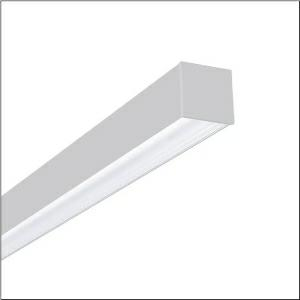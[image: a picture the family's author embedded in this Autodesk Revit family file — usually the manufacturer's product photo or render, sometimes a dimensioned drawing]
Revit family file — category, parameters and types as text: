
# Revit family: silica_r_5mx31bd1w4a_74d2
name_source: partatom
category: Lighting Fixtures
units: mm (PartAtom-declared; Revit-internal decimal feet)

## family parameters
Cut with Voids When Loaded = No
Host = Face
Light Source = No
Part Type = Normal
Room Calculation Point = No
Round Connector Dimension = Use Diameter
Shared = No

## types (1)
- --- (1 x LED, 7070 lm, 45.6 W, 4000K)
    Apparent Load = 46 VA
    CIE Flux Codes = 82 97 100 70 100
    Color Rendering = 80
    Color Temperature = 4000K
    Default Elevation = 1800 mm
    Description = Silica®, office luminaire, of aluminium, light emission: direct/indirect distribution, primary light characteristic: symmetric, installation type: suspended mounting, LED rated luminous flux: 7.070 lm, light colour: 840, colour temperature: 4000K, control gear: ECG DALI, with terminal, 3+2-pole, max. 2.5mm², mains connection: 230V, AC, 50/60Hz, connection cable inclusive, cable length: 1,5 m, rated input power: 46W, luminaire housing, of aluminium, traffic white (RAL 9016), length: 1.442 mm, width: 65 mm, height: 64mm, protection rating (complete): IP20, insulation class (complete): insulation class I (protective earthing), certification: CE, permissible ambient temperature for indoor applications: 0..+35°C, standard: EN 50419, packaging unit: 1 piece
    Height = 64 mm
    Lamp = 1 x LED
    Lamp Light Flux = 7070 lm
    Lamp Power = 45.6 W
    Lamp count = 1
    Length = 1442 mm
    Luminous efficacy = 155 lm/W
    Manufacturer = Siteco
    ModVariant = No
    Model = 5MX31BD1W4A
    Mounting Place = Ceiling
    Mounting Type = Pendant
    Number of Poles = 1
    OnlyDefault = Yes
    Power Factor = 1
    Product Name = Silica®
    Product group = office luminaire | ceiling pendant
    ProductGroupID = 905
    Protection Class = Protection class I
    Protection Degree = IP 20
    RLX_Detail_Level = 1
    RlxData = <blob elided: 28893 chars, md5=2de192fa>
    Socket = socket
    Standby Power = 0 W
    System Light Flux = 7070 lm
    System Power = 46 W
    Type Comments = factory setting: direct and indirect light
    Type Image = l_1003924.jpg
    URL = http://relux.com
    VarID = @adj_131726
    Voltage = 0 V
    Weight = 0.00 kg
    Width = 66 mm

## geometry (parser evidence)
native form markers: Blend x4, Sweep x12
no freeform markers — native parametric forms only
